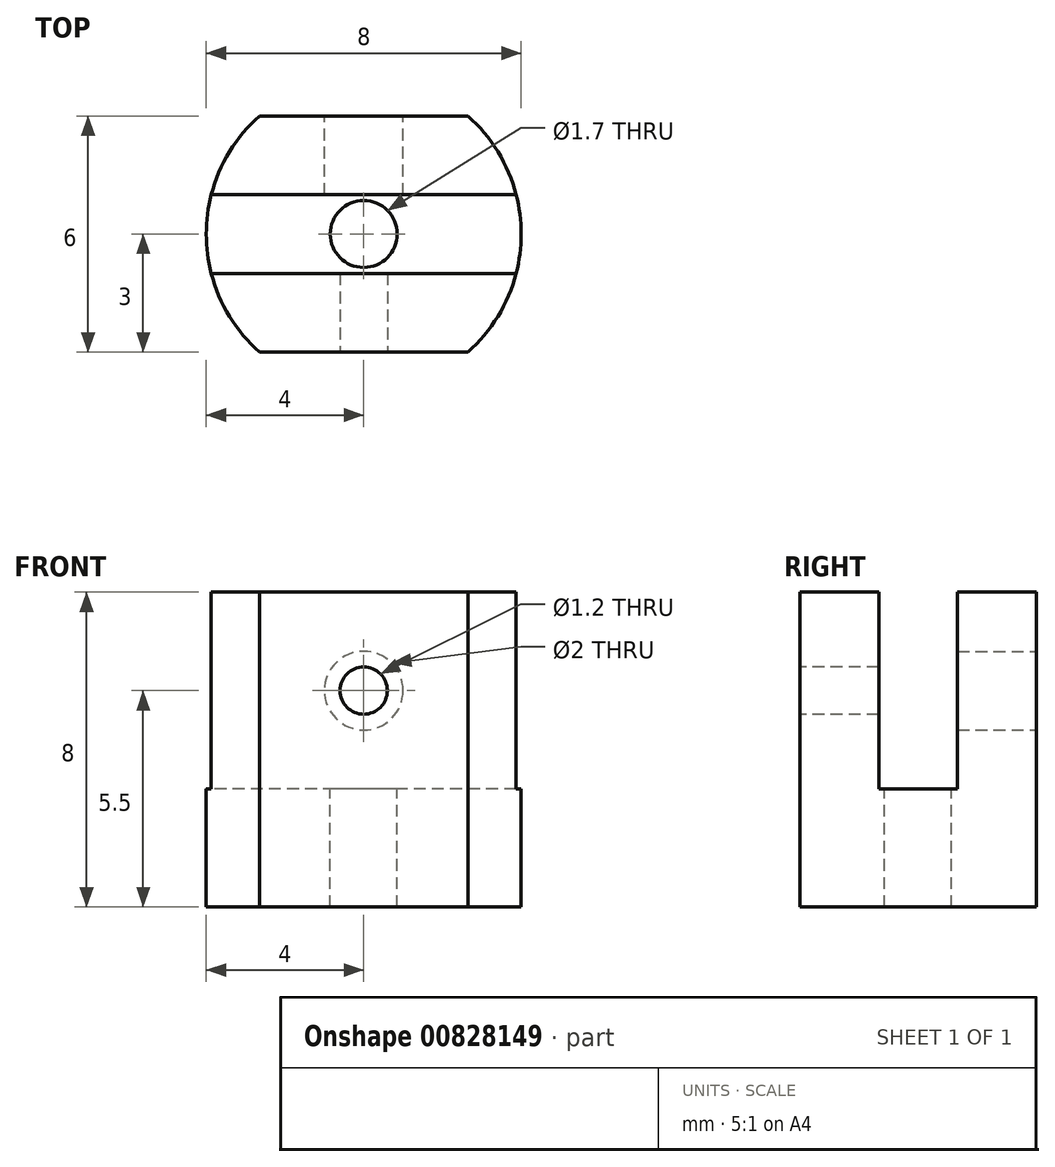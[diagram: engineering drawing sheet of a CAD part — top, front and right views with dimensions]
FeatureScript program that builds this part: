
annotation { "Feature Type Name" : "Feature", "Feature Type Description" : "" }
export const myFeature = defineFeature(function(context is Context, id is Id, definition is map)
    precondition{}
    {
        {
            var Q0;
            Q0=qCreatedBy(makeId("Top.planeOp"),FACE);
            var sketch = newSketch(context, id + "F0", { "sketchPlane" : qUnion([Q0])});
            skArc(sketch, "E0", {"start": v(-2.65, 3) * mm, "mid": v(-4, 0) * mm, "end": v(-2.65, -3) * mm});
            skLineSegment(sketch, "E1.bottom", {"start": v(-2.65, 3) * mm, "end": v(2.65, 3) * mm});
            skLineSegment(sketch, "E1.top", {"start": v(-2.65, -3) * mm, "end": v(2.65, -3) * mm});
            skArc(sketch, "E2.trimOffspring", {"start": v(2.65, -3) * mm, "mid": v(4, 0) * mm, "end": v(2.65, 3) * mm});
            skSolve(sketch);
        }
        {
            var Q0;
            Q0 = qSketchRegion(id + "F0", true);
            extrude(context, id + "F1", {"entities" : qUnion([Q0]), "depth" : 8 * mm, "offsetDistance" : 25 * mm});
        }
        {
            var Q0;
            Q0=makeQuery(id+"F1.opExtrude","CAP_FACE",FACE,{"disambiguationData":[OSD([sQuery(id+"F0.wireOp",EDGE,"E0"),sQuery(id+"F0.wireOp",EDGE,"E1.bottom"),sQuery(id+"F0.wireOp",EDGE,"E1.top"),sQuery(id+"F0.wireOp",EDGE,"E2.trimOffspring")])],"isStart":false});
            var sketch = newSketch(context, id + "F2", { "sketchPlane" : qUnion([Q0])});
            skLineSegment(sketch, "E3.bottom", {"start": v(4.58, 1) * mm, "end": v(-4.58, 1) * mm});
            skLineSegment(sketch, "E3.top", {"start": v(4.58, -1) * mm, "end": v(-4.58, -1) * mm});
            skLineSegment(sketch, "E3.left", {"start": v(4.58, 1) * mm, "end": v(4.58, -1) * mm});
            skLineSegment(sketch, "E3.right", {"start": v(-4.58, 1) * mm, "end": v(-4.58, -1) * mm});
            skPoint(sketch, "E3.middle", {"position": v(0, 0) * mm});
            skSolve(sketch);
        }
        {
            var Q0;
            Q0 = qSketchRegion(id + "F2", true);
            extrude(context, id + "F3", {"entities" : qUnion([Q0]), "operationType" : NewBodyOperationType.REMOVE, "oppositeDirection" : true, "depth" : 5 * mm, "offsetDistance" : 25 * mm});
        }
        {
            var Q0;
            Q0=makeQuery(id+"F1.opExtrude","SWEPT_FACE",FACE,{"disambiguationData":[OSD([sQuery(id+"F0.wireOp",EDGE,"E1.top")])]});
            var sketch = newSketch(context, id + "F4", { "sketchPlane" : qUnion([Q0])});
            skCircle(sketch, "E4", {"center": v(0, 5.5) * mm, "radius": 0.6 * mm});
            skSolve(sketch);
        }
        {
            var Q0;
            Q0 = qSketchRegion(id + "F4", true);
            extrude(context, id + "F5", {"entities" : qUnion([Q0]), "operationType" : NewBodyOperationType.REMOVE, "endBound" : BoundingType.THROUGH_ALL, "oppositeDirection" : true, "depth" : 25 * mm, "offsetDistance" : 25 * mm});
        }
        {
            var Q0;
            Q0=makeQuery(id+"F1.opExtrude","SWEPT_FACE",FACE,{"disambiguationData":[OSD([sQuery(id+"F0.wireOp",EDGE,"E1.bottom")])]});
            var sketch = newSketch(context, id + "F6", { "sketchPlane" : qUnion([Q0])});
            skCircle(sketch, "E5", {"center": v(0, 5.5) * mm, "radius": 1 * mm});
            skSolve(sketch);
        }
        {
            var Q0;
            Q0 = qSketchRegion(id + "F6", true);
            var Q1;
            Q1=makeQuery(id+"F3.boolean.opBoolean","COPY",FACE,{"derivedFrom":makeQuery(id+"F3.opExtrude","SWEPT_FACE",FACE,{"disambiguationData":[OSD([sQuery(id+"F2.wireOp",EDGE,"E3.bottom")])]})});
            extrude(context, id + "F7", {"entities" : qUnion([Q0]), "operationType" : NewBodyOperationType.REMOVE, "endBound" : BoundingType.UP_TO_SURFACE, "oppositeDirection" : true, "depth" : 25 * mm, "endBoundEntityFace" : qUnion([Q1]), "offsetDistance" : 25 * mm});
        }
        {
            var Q0;
            Q0=makeQuery(id+"F3.boolean.opBoolean","COPY",FACE,{"derivedFrom":makeQuery(id+"F3.opExtrude","CAP_FACE",FACE,{"disambiguationData":[OSD([sQuery(id+"F2.wireOp",EDGE,"E3.bottom"),sQuery(id+"F2.wireOp",EDGE,"E3.top"),sQuery(id+"F2.wireOp",EDGE,"E3.left"),sQuery(id+"F2.wireOp",EDGE,"E3.right")])],"isStart":false})});
            var sketch = newSketch(context, id + "F8", { "sketchPlane" : qUnion([Q0])});
            skCircle(sketch, "E6", {"center": v(0, 0) * mm, "radius": 0.85 * mm});
            skSolve(sketch);
        }
        {
            var Q0;
            Q0 = qSketchRegion(id + "F8", true);
            extrude(context, id + "F9", {"entities" : qUnion([Q0]), "operationType" : NewBodyOperationType.REMOVE, "endBound" : BoundingType.THROUGH_ALL, "oppositeDirection" : true, "depth" : 25 * mm, "offsetDistance" : 25 * mm});
        }
    });
